# Revit family: Trägeranbindung IB vertikal, Typ D III
name_source: partatom
category: HLS-Bauteile
units: mm (PartAtom-declared; Revit-internal decimal feet)

## family parameters
Arbeitsebenenbasiert = Ja
Beim Laden mit Abzugskörper schneiden = Nein
Bemaßung runder Anschluss = Durchmesser verwenden
Beschriftungsausrichtung beibehalten = Nein
Gemeinsam genutzt = Ja
Immer vertikal = Nein
Raumberechnungspunkt = Nein
Teiletyp = Normal

## types (1)
- Trägeranbindung IB vertikal, Typ D III
    Artikelnummer = 08146103
    EAN = 4250928420084
    Fabrikat = MEFA
    Firma = MEFA Befestigungs- und Montagesysteme GmbH
    Gewicht = 1.13 kg
    Gewicht pro Bauteil = 1.13 kg
    Gewindestangentyp = M12x310
    Klemmweite = 100-220 mm
    Klemmweite Flansch max. = 220 mm
    Klemmweite Flansch min. = 100 mm  [stored 0.328084 ft]
    Kurztext1 = Trägeranbindung IB C-Profil 45
    Kurztext2 = Typ D III Klemmdicke 8 - 15 mm
    Länge Gewindestange = 310 mm  [stored 1.01706 ft]
    Material = Stahl
    Materialname = S235
    Mengeneinheit = St
    Oberflaeche = feuerstückverzinkt
    Typ = D III
    Vorgabe-Ansicht = 1219 mm
    max Klemmdicke = 15 mm  [stored 0.0492126 ft]
    max. Klemmstärke = 0 mm  [stored 0 ft]
    max. Klemmweite = 220 mm
    min. Klemmdicke = 8 mm
    vpe = 1

note: [stored X ft] marks values corroborated as IEEE doubles in the binary element streams (Revit-internal decimal feet)

## geometry (parser evidence)
native form markers: Sweep x2
no freeform markers — native parametric forms only
